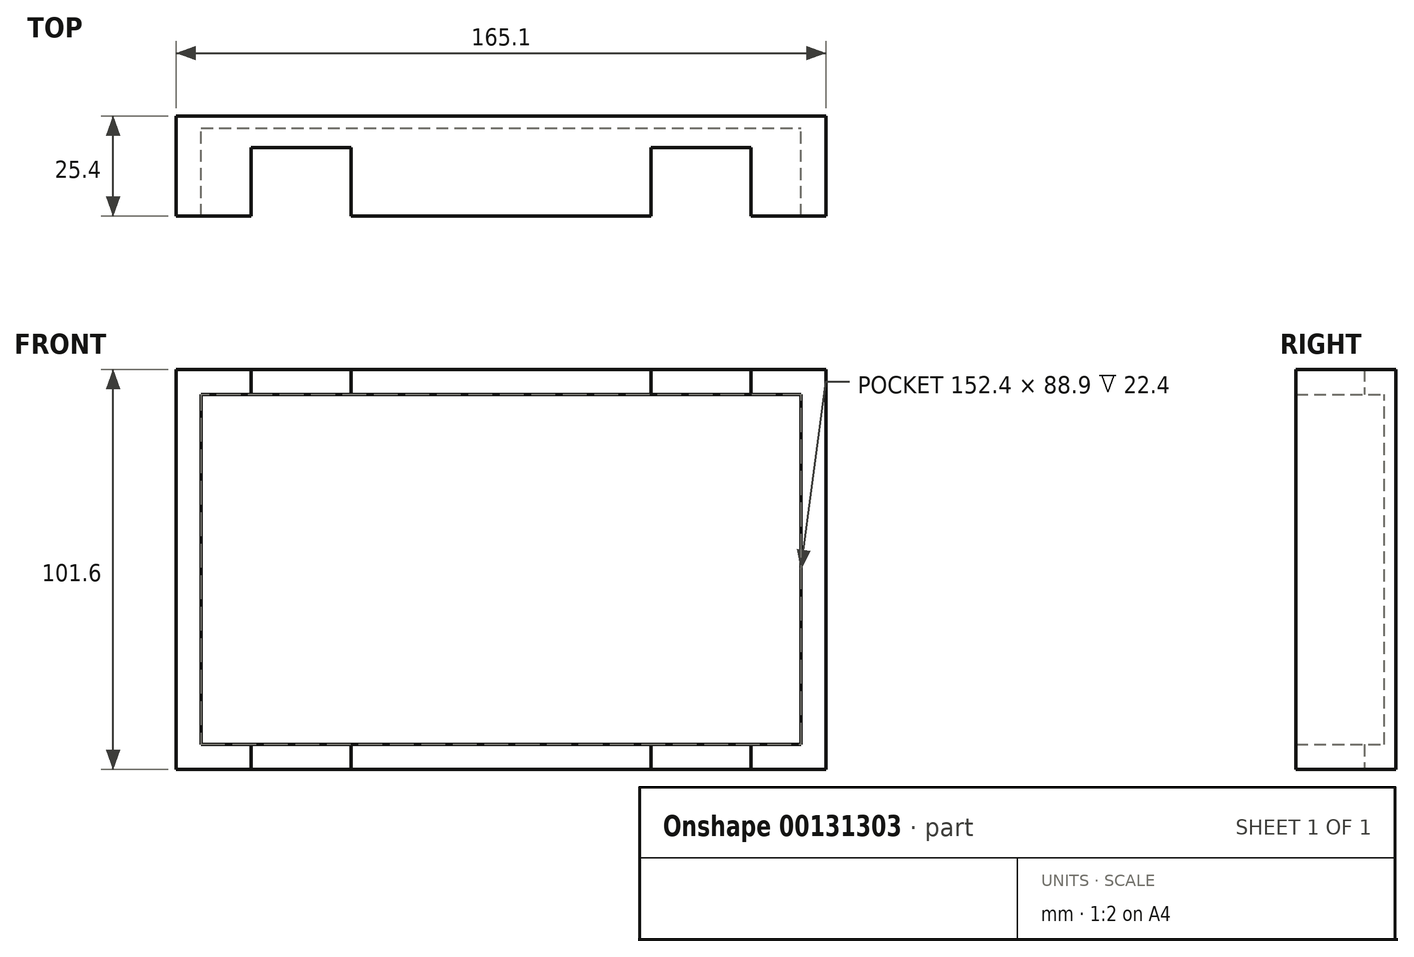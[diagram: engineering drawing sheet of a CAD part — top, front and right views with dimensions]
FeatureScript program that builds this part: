
annotation { "Feature Type Name" : "Feature", "Feature Type Description" : "" }
export const myFeature = defineFeature(function(context is Context, id is Id, definition is map)
    precondition{}
    {
        {
            var Q0;
            Q0=qCreatedBy(makeId("Front.planeOp"),FACE);
            var sketch = newSketch(context, id + "F0", { "sketchPlane" : qUnion([Q0])});
            skLineSegment(sketch, "E0.bottom", {"start": v(-62.53, 61.49) * mm, "end": v(102.57, 61.49) * mm});
            skLineSegment(sketch, "E0.top", {"start": v(-62.53, -40.11) * mm, "end": v(102.57, -40.11) * mm});
            skLineSegment(sketch, "E0.left", {"start": v(-62.53, 61.49) * mm, "end": v(-62.53, -40.11) * mm});
            skLineSegment(sketch, "E0.right", {"start": v(102.57, 61.49) * mm, "end": v(102.57, -40.11) * mm});
            skLineSegment(sketch, "E1", {"start": v(-56.18, 61.49) * mm, "end": v(-56.18, -40.11) * mm, "construction": true});
            skLineSegment(sketch, "E2", {"start": v(-62.53, 55.14) * mm, "end": v(102.57, 55.14) * mm});
            skLineSegment(sketch, "E3", {"start": v(96.22, 61.49) * mm, "end": v(96.22, -40.11) * mm});
            skLineSegment(sketch, "E4", {"start": v(102.57, -33.76) * mm, "end": v(-62.53, -33.76) * mm});
            skLineSegment(sketch, "E5", {"start": v(83.52, 61.49) * mm, "end": v(83.52, 55.14) * mm});
            skLineSegment(sketch, "E6", {"start": v(58.12, 61.49) * mm, "end": v(58.12, 55.14) * mm});
            skLineSegment(sketch, "E7", {"start": v(-43.48, 61.49) * mm, "end": v(-43.48, 55.14) * mm});
            skLineSegment(sketch, "E8", {"start": v(-18.08, 61.49) * mm, "end": v(-18.08, 55.14) * mm});
            skLineSegment(sketch, "E9", {"start": v(-43.48, -33.76) * mm, "end": v(-43.48, -40.11) * mm});
            skLineSegment(sketch, "E10", {"start": v(-18.08, -40.11) * mm, "end": v(-18.08, -33.76) * mm});
            skLineSegment(sketch, "E11", {"start": v(83.52, -33.76) * mm, "end": v(83.52, -40.11) * mm});
            skLineSegment(sketch, "E12", {"start": v(58.12, -33.76) * mm, "end": v(58.12, -40.11) * mm});
            skLineSegment(sketch, "E13", {"start": v(-18.08, 61.49) * mm, "end": v(-18.08, -56.77) * mm, "construction": true});
            skLineSegment(sketch, "E14", {"start": v(58.12, 61.49) * mm, "end": v(58.12, -38.26) * mm, "construction": true});
            skPoint(sketch, "E14.endSnap0", {"position": v(58.12, -36.94) * mm});
            skLineSegment(sketch, "E15", {"start": v(83.52, 61.49) * mm, "end": v(83.52, -57.98) * mm, "construction": true});
            skLineSegment(sketch, "E16", {"start": v(-43.6, 41.5) * mm, "end": v(-43.48, -58.58) * mm, "construction": true});
            skLineSegment(sketch, "E17", {"start": v(-56.18, -40.11) * mm, "end": v(-56.18, 61.49) * mm});
            skSolve(sketch);
        }
        {
            var Q0;
            {var subQ4=sQuery(id+"F0.wireOp",EDGE,"E2");var subQ10=sQuery(id+"F0.wireOp",EDGE,"E1");var subQ11=makeQuery(id+"F0.imprint","INTERSECT",VERTEX,{"derivedFrom":[subQ10,subQ4]});Q0=makeQuery(id+"F0.imprint","IMPRINT",FACE,{"disambiguationData":[TD([[makeQuery(id+"F0.imprint","IMPRINT",EDGE,{"disambiguationData":[TD([[subQ11,-1.0]])],"derivedFrom":subQ10}),1.0]])]});}
            var Q1;
            {var subQ3=sQuery(id+"F0.wireOp",EDGE,"E2");var subQ14=makeQuery(id+"F0.imprint","INTERSECT",VERTEX,{"derivedFrom":[subQ3,sQuery(id+"F0.wireOp",EDGE,"E7")]});Q1=makeQuery(id+"F0.imprint","IMPRINT",FACE,{"disambiguationData":[TD([[makeQuery(id+"F0.imprint","IMPRINT",EDGE,{"disambiguationData":[TD([[subQ14,1.0]])],"derivedFrom":subQ3}),-1.0]])]});}
            extrude(context, id + "F1", {"entities" : qUnion([Q0, Q1]), "depth" : 3 * mm});
        }
        {
            var Q0;
            {var subQ0=sQuery(id+"F0.wireOp",EDGE,"E0.left");var subQ1=sQuery(id+"F0.wireOp",EDGE,"E0.bottom");var subQ2=makeQuery(id+"F0.imprint","INTERSECT",VERTEX,{"derivedFrom":[subQ1,subQ0]});Q0=makeQuery(id+"F0.imprint","IMPRINT",FACE,{"disambiguationData":[TD([[makeQuery(id+"F0.imprint","IMPRINT",EDGE,{"disambiguationData":[TD([[subQ2,-1.0]])],"derivedFrom":subQ1}),-1.0]])]});}
            var Q1;
            {var subQ0=sQuery(id+"F0.wireOp",EDGE,"E0.right");var subQ1=sQuery(id+"F0.wireOp",EDGE,"E0.bottom");var subQ2=makeQuery(id+"F0.imprint","INTERSECT",VERTEX,{"derivedFrom":[subQ1,subQ0]});Q1=makeQuery(id+"F0.imprint","IMPRINT",FACE,{"disambiguationData":[TD([[makeQuery(id+"F0.imprint","IMPRINT",EDGE,{"disambiguationData":[TD([[subQ2,1.0]])],"derivedFrom":subQ1}),-1.0]])]});}
            var Q2;
            {var subQ0=sQuery(id+"F0.wireOp",EDGE,"E0.left");var subQ1=sQuery(id+"F0.wireOp",EDGE,"E0.top");var subQ2=makeQuery(id+"F0.imprint","INTERSECT",VERTEX,{"derivedFrom":[subQ1,subQ0]});Q2=makeQuery(id+"F0.imprint","IMPRINT",FACE,{"disambiguationData":[TD([[makeQuery(id+"F0.imprint","IMPRINT",EDGE,{"disambiguationData":[TD([[subQ2,-1.0]])],"derivedFrom":subQ1}),1.0]])]});}
            var Q3;
            {var subQ0=sQuery(id+"F0.wireOp",EDGE,"E0.right");var subQ1=sQuery(id+"F0.wireOp",EDGE,"E0.top");var subQ2=makeQuery(id+"F0.imprint","INTERSECT",VERTEX,{"derivedFrom":[subQ1,subQ0]});Q3=makeQuery(id+"F0.imprint","IMPRINT",FACE,{"disambiguationData":[TD([[makeQuery(id+"F0.imprint","IMPRINT",EDGE,{"disambiguationData":[TD([[subQ2,1.0]])],"derivedFrom":subQ1}),1.0]])]});}
            var Q4;
            {var subQ3=sQuery(id+"F0.wireOp",EDGE,"E7");Q4=makeQuery(id+"F0.imprint","IMPRINT",FACE,{"disambiguationData":[TD([[makeQuery(id+"F0.imprint","IMPRINT",EDGE,{"derivedFrom":subQ3}),-1.0]])]});}
            var Q5;
            {var subQ0=sQuery(id+"F0.wireOp",EDGE,"E6");Q5=makeQuery(id+"F0.imprint","IMPRINT",FACE,{"disambiguationData":[TD([[makeQuery(id+"F0.imprint","IMPRINT",EDGE,{"derivedFrom":subQ0}),-1.0]])]});}
            var Q6;
            {var subQ3=sQuery(id+"F0.wireOp",EDGE,"E5");Q6=makeQuery(id+"F0.imprint","IMPRINT",FACE,{"disambiguationData":[TD([[makeQuery(id+"F0.imprint","IMPRINT",EDGE,{"derivedFrom":subQ3}),1.0]])]});}
            var Q7;
            {var subQ3=sQuery(id+"F0.wireOp",EDGE,"E9");Q7=makeQuery(id+"F0.imprint","IMPRINT",FACE,{"disambiguationData":[TD([[makeQuery(id+"F0.imprint","IMPRINT",EDGE,{"derivedFrom":subQ3}),-1.0]])]});}
            var Q8;
            {var subQ0=sQuery(id+"F0.wireOp",EDGE,"E10");Q8=makeQuery(id+"F0.imprint","IMPRINT",FACE,{"disambiguationData":[TD([[makeQuery(id+"F0.imprint","IMPRINT",EDGE,{"derivedFrom":subQ0}),-1.0]])]});}
            var Q9;
            {var subQ3=sQuery(id+"F0.wireOp",EDGE,"E11");Q9=makeQuery(id+"F0.imprint","IMPRINT",FACE,{"disambiguationData":[TD([[makeQuery(id+"F0.imprint","IMPRINT",EDGE,{"derivedFrom":subQ3}),1.0]])]});}
            var Q10;
            {var subQ0=sQuery(id+"F0.wireOp",EDGE,"E2");var subQ1=sQuery(id+"F0.wireOp",EDGE,"E0.right");var subQ2=makeQuery(id+"F0.imprint","INTERSECT",VERTEX,{"derivedFrom":[subQ1,subQ0]});Q10=makeQuery(id+"F0.imprint","IMPRINT",FACE,{"disambiguationData":[TD([[makeQuery(id+"F0.imprint","IMPRINT",EDGE,{"disambiguationData":[TD([[subQ2,-1.0]])],"derivedFrom":subQ1}),-1.0]])]});}
            var Q11;
            {var subQ0=sQuery(id+"F0.wireOp",EDGE,"E2");var subQ1=sQuery(id+"F0.wireOp",EDGE,"E0.left");var subQ2=makeQuery(id+"F0.imprint","INTERSECT",VERTEX,{"derivedFrom":[subQ1,subQ0]});Q11=makeQuery(id+"F0.imprint","IMPRINT",FACE,{"disambiguationData":[TD([[makeQuery(id+"F0.imprint","IMPRINT",EDGE,{"disambiguationData":[TD([[subQ2,-1.0]])],"derivedFrom":subQ1}),1.0]])]});}
            extrude(context, id + "F2", {"entities" : qUnion([Q0, Q1, Q2, Q3, Q4, Q5, Q6, Q7, Q8, Q9, Q10, Q11]), "operationType" : NewBodyOperationType.ADD, "depth" : 25.4 * mm});
        }
        {
            var Q0;
            {var subQ0=sQuery(id+"F0.wireOp",EDGE,"E9");Q0=makeQuery(id+"F0.imprint","IMPRINT",FACE,{"disambiguationData":[TD([[makeQuery(id+"F0.imprint","IMPRINT",EDGE,{"derivedFrom":subQ0}),1.0]])]});}
            var Q1;
            {var subQ0=sQuery(id+"F0.wireOp",EDGE,"E7");Q1=makeQuery(id+"F0.imprint","IMPRINT",FACE,{"disambiguationData":[TD([[makeQuery(id+"F0.imprint","IMPRINT",EDGE,{"derivedFrom":subQ0}),1.0]])]});}
            var Q2;
            {var subQ0=sQuery(id+"F0.wireOp",EDGE,"E5");Q2=makeQuery(id+"F0.imprint","IMPRINT",FACE,{"disambiguationData":[TD([[makeQuery(id+"F0.imprint","IMPRINT",EDGE,{"derivedFrom":subQ0}),-1.0]])]});}
            var Q3;
            {var subQ0=sQuery(id+"F0.wireOp",EDGE,"E11");Q3=makeQuery(id+"F0.imprint","IMPRINT",FACE,{"disambiguationData":[TD([[makeQuery(id+"F0.imprint","IMPRINT",EDGE,{"derivedFrom":subQ0}),-1.0]])]});}
            extrude(context, id + "F3", {"entities" : qUnion([Q0, Q1, Q2, Q3]), "operationType" : NewBodyOperationType.ADD, "depth" : 8 * mm});
        }
    });
